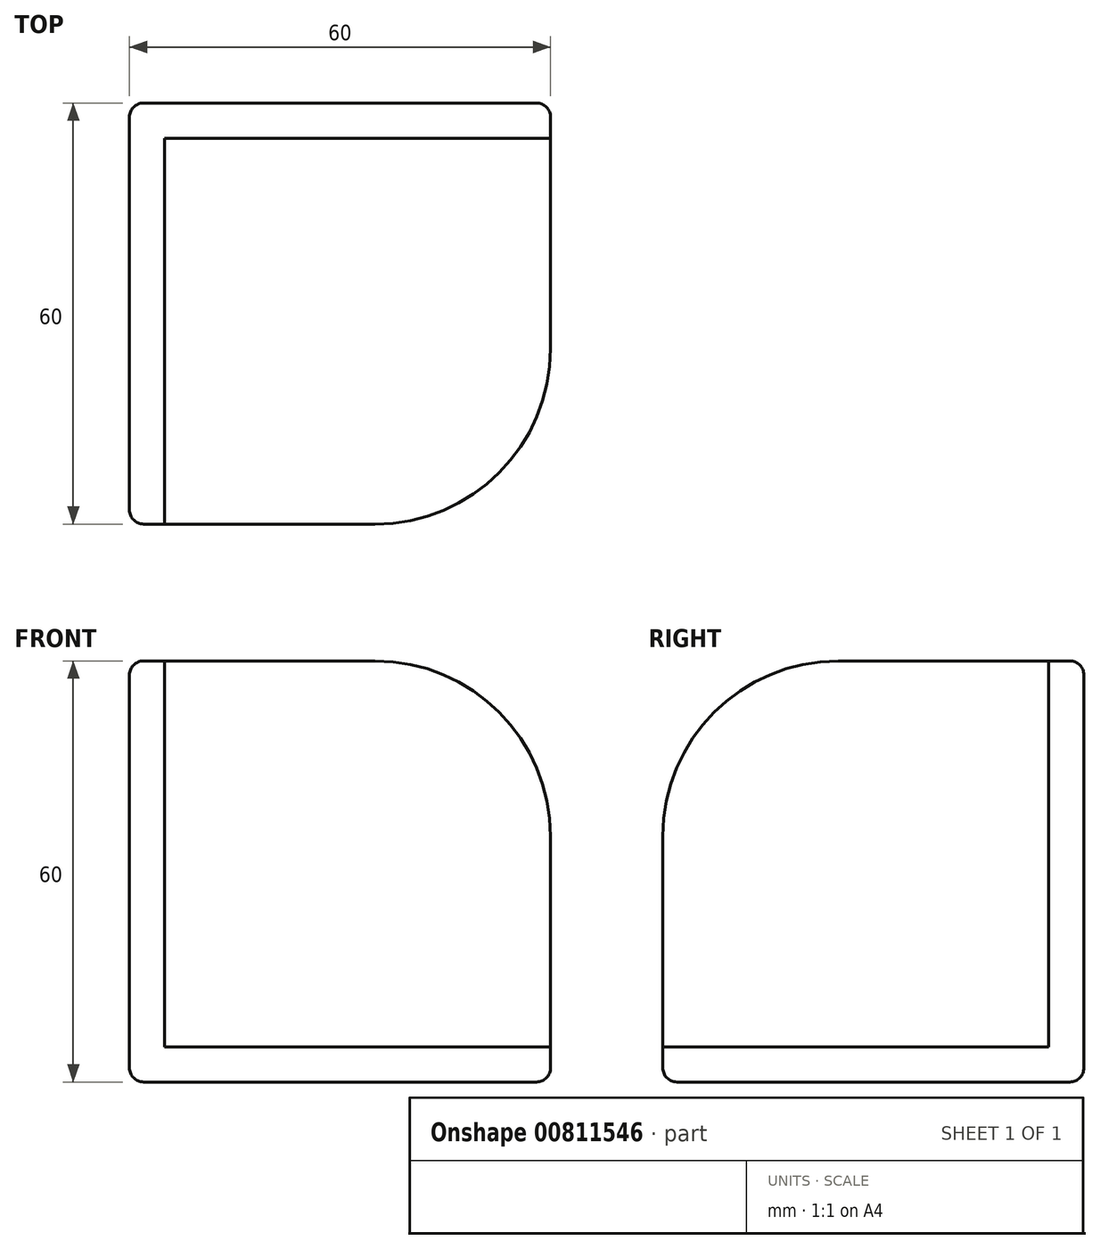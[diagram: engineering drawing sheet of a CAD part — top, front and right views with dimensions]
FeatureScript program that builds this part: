
annotation { "Feature Type Name" : "Feature", "Feature Type Description" : "" }
export const myFeature = defineFeature(function(context is Context, id is Id, definition is map)
    precondition{}
    {
        {
            var Q0;
            Q0=qCreatedBy(makeId("Top.planeOp"),FACE);
            var sketch = newSketch(context, id + "F0", { "sketchPlane" : qUnion([Q0])});
            skLineSegment(sketch, "E0.bottom", {"start": v(30, -30) * mm, "end": v(-30, -30) * mm});
            skLineSegment(sketch, "E0.top", {"start": v(30, 30) * mm, "end": v(-30, 30) * mm});
            skLineSegment(sketch, "E0.left", {"start": v(30, -30) * mm, "end": v(30, 30) * mm});
            skLineSegment(sketch, "E0.right", {"start": v(-30, -30) * mm, "end": v(-30, 30) * mm});
            skPoint(sketch, "E0.middle", {"position": v(0, 0) * mm});
            skSolve(sketch);
        }
        {
            var Q0;
            Q0=makeQuery(id+"F0.imprint","IMPRINT",FACE,{"disambiguationData":[TD([[makeQuery(id+"F0.imprint","IMPRINT",EDGE,{"derivedFrom":sQuery(id+"F0.wireOp",EDGE,"E0.bottom")}),-1.0]])]});
            extrude(context, id + "F1", {"entities" : qUnion([Q0]), "depth" : 5 * mm, "offsetDistance" : 25 * mm});
        }
        {
            var Q0;
            Q0=makeQuery(id+"F1.opExtrude","CAP_FACE",FACE,{"disambiguationData":[OSD([sQuery(id+"F0.wireOp",EDGE,"E0.bottom"),sQuery(id+"F0.wireOp",EDGE,"E0.top"),sQuery(id+"F0.wireOp",EDGE,"E0.left"),sQuery(id+"F0.wireOp",EDGE,"E0.right")])],"isStart":false});
            var sketch = newSketch(context, id + "F2", { "sketchPlane" : qUnion([Q0])});
            skLineSegment(sketch, "E1.bottom", {"start": v(-30, 30) * mm, "end": v(-25, 30) * mm});
            skLineSegment(sketch, "E1.top", {"start": v(-30, -30) * mm, "end": v(-25, -30) * mm});
            skLineSegment(sketch, "E1.left", {"start": v(-30, 30) * mm, "end": v(-30, -30) * mm});
            skLineSegment(sketch, "E1.right", {"start": v(-25, 30) * mm, "end": v(-25, -30) * mm});
            skLineSegment(sketch, "E2.bottom", {"start": v(-25, 30) * mm, "end": v(30, 30) * mm});
            skLineSegment(sketch, "E2.top", {"start": v(-25, 25) * mm, "end": v(30, 25) * mm});
            skLineSegment(sketch, "E2.left", {"start": v(-25, 30) * mm, "end": v(-25, 25) * mm});
            skLineSegment(sketch, "E2.right", {"start": v(30, 30) * mm, "end": v(30, 25) * mm});
            skSolve(sketch);
        }
        {
            var Q0;
            Q0=qSketchRegion(id+"F2",true);
            extrude(context, id + "F3", {"entities" : qUnion([Q0]), "operationType" : NewBodyOperationType.ADD, "depth" : 55 * mm, "offsetDistance" : 25 * mm});
        }
        {
            var Q0;
            Q0=makeQuery(id+"F3.opExtrude","CAP_EDGE",EDGE,{"disambiguationData":[OSD([sQuery(id+"F2.wireOp",EDGE,"E2.right")])],"isStart":false});
            var Q1;
            Q1=makeQuery(id+"F3.opExtrude","CAP_EDGE",EDGE,{"disambiguationData":[OSD([sQuery(id+"F2.wireOp",EDGE,"E1.top")])],"isStart":false});
            var Q2;
            Q2=makeQuery(id+"F1.opExtrude","SWEPT_EDGE",EDGE,{"disambiguationData":[OSD([sQuery(id+"F0.wireOp",EDGE,"E0.bottom"),sQuery(id+"F0.wireOp",EDGE,"E0.left")])]});
            fillet(context, id + "F4", {"entities" : qUnion([Q0, Q1, Q2]), "radius" : 25 * mm, "tangentPropagation" : true, "allowEdgeOverflow" : false});
        }
        {
            var Q0;
            Q0=makeQuery(id+"F1.opExtrude","CAP_FACE",FACE,{"disambiguationData":[OSD([sQuery(id+"F0.wireOp",EDGE,"E0.bottom"),sQuery(id+"F0.wireOp",EDGE,"E0.top"),sQuery(id+"F0.wireOp",EDGE,"E0.left"),sQuery(id+"F0.wireOp",EDGE,"E0.right")])],"isStart":true});
            var Q1;
            Q1=makeQuery(id+"F3.boolean.opBoolean","MERGE",FACE,{"derivedFrom":[makeQuery(id+"F1.opExtrude","SWEPT_FACE",FACE,{"disambiguationData":[OSD([sQuery(id+"F0.wireOp",EDGE,"E0.right")])]}),makeQuery(id+"F3.opExtrude","SWEPT_FACE",FACE,{"disambiguationData":[OSD([sQuery(id+"F2.wireOp",EDGE,"E1.left")])]})]});
            var Q2;
            Q2=makeQuery(id+"F3.boolean.opBoolean","MERGE",FACE,{"derivedFrom":[makeQuery(id+"F1.opExtrude","SWEPT_FACE",FACE,{"disambiguationData":[OSD([sQuery(id+"F0.wireOp",EDGE,"E0.top")])]}),makeQuery(id+"F3.opExtrude","SWEPT_FACE",FACE,{"disambiguationData":[OSD([sQuery(id+"F2.wireOp",EDGE,"E1.bottom"),sQuery(id+"F2.wireOp",EDGE,"E2.bottom")])]})]});
            fillet(context, id + "F5", {"entities" : qUnion([Q0, Q1, Q2]), "radius" : 2 * mm, "tangentPropagation" : true, "allowEdgeOverflow" : false});
        }
    });
